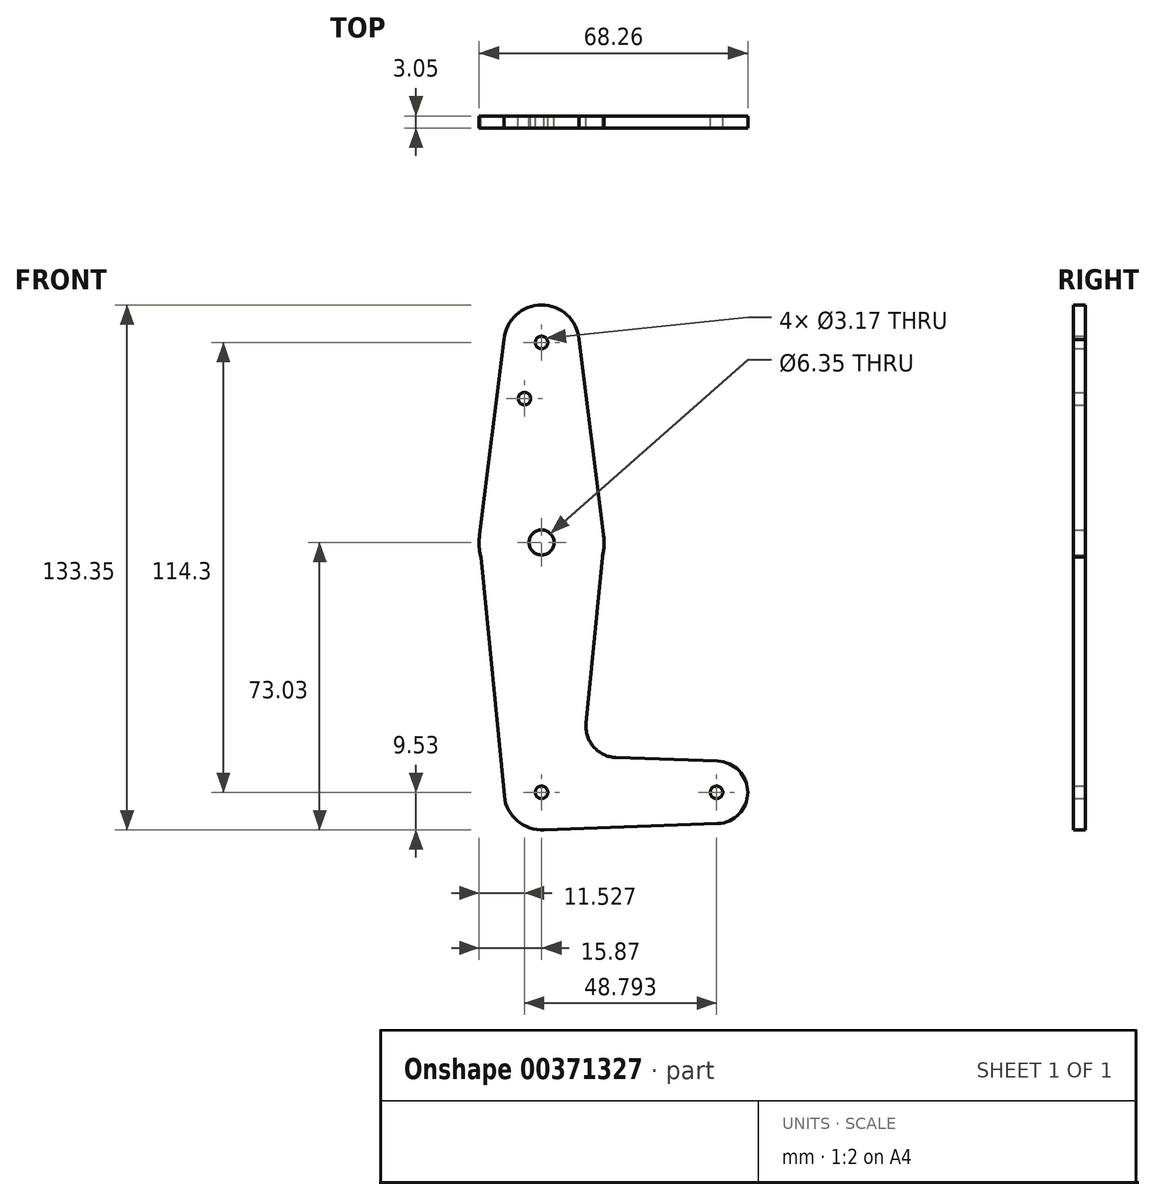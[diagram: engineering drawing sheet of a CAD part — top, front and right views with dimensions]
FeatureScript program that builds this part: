
annotation { "Feature Type Name" : "Feature", "Feature Type Description" : "" }
export const myFeature = defineFeature(function(context is Context, id is Id, definition is map)
    precondition{}
    {
        {
            var Q0;
            Q0=qCreatedBy(makeId("Front.planeOp"),FACE);
            var sketch = newSketch(context, id + "F0", { "sketchPlane" : qUnion([Q0])});
            skLineSegment(sketch, "E0", {"start": v(0, 50.8) * mm, "end": v(0, -63.5) * mm});
            skLineSegment(sketch, "E1", {"start": v(0, -63.5) * mm, "end": v(44.45, -63.5) * mm});
            skCircle(sketch, "E2", {"center": v(0, 0) * mm, "radius": 15.88 * mm});
            skCircle(sketch, "E3", {"center": v(0, 50.8) * mm, "radius": 9.53 * mm});
            skCircle(sketch, "E4", {"center": v(0, -63.5) * mm, "radius": 9.53 * mm});
            skCircle(sketch, "E5", {"center": v(44.45, -63.5) * mm, "radius": 7.94 * mm});
            skLineSegment(sketch, "E6", {"start": v(-9.4, 52.39) * mm, "end": v(-16, 0) * mm});
            skLineSegment(sketch, "E7", {"start": v(9.4, 52.39) * mm, "end": v(16, 0) * mm});
            skLineSegment(sketch, "E8", {"start": v(-15.44, -3.7) * mm, "end": v(-9.48, -64.43) * mm});
            skLineSegment(sketch, "E9", {"start": v(18.92, -54.65) * mm, "end": v(44.73, -55.57) * mm});
            skLineSegment(sketch, "E10", {"start": v(0, -73.02) * mm, "end": v(44.73, -71.43) * mm});
            skPoint(sketch, "E11.orphan", {"position": v(16, -3.7) * mm});
            skLineSegment(sketch, "E12.MirrorCS", {"start": v(15.44, -3.7) * mm, "end": v(11.3, -45.93) * mm});
            skCircle(sketch, "E13", {"center": v(-4.34, 36.53) * mm, "radius": 1.59 * mm});
            skCircle(sketch, "E14", {"center": v(0, 0) * mm, "radius": 3.18 * mm});
            skCircle(sketch, "E15", {"center": v(0, -63.5) * mm, "radius": 1.59 * mm});
            skCircle(sketch, "E16", {"center": v(44.45, -63.5) * mm, "radius": 1.59 * mm});
            skPoint(sketch, "E17.newPointB", {"position": v(9.48, -64.43) * mm});
            skArc(sketch, "E17.filletArc", {"start": v(11.3, -45.93) * mm, "mid": v(13.22, -51.94) * mm, "end": v(18.92, -54.65) * mm});
            skCircle(sketch, "E18", {"center": v(0, 50.8) * mm, "radius": 1.59 * mm});
            skSolve(sketch);
        }
        {
            var Q0;
            Q0 = qSketchRegion(id + "F0", true);
            var Q1;
            {var subQ0=sQuery(id+"F0.wireOp",EDGE,"E4");var subQ1=sQuery(id+"F0.wireOp",EDGE,"E0");var subQ2=makeQuery(id+"F0.imprint","INTERSECT",VERTEX,{"derivedFrom":[subQ1,subQ0]});Q1=makeQuery(id+"F0.imprint","IMPRINT",FACE,{"disambiguationData":[TD([[makeQuery(id+"F0.imprint","IMPRINT",EDGE,{"disambiguationData":[TD([[subQ2,-1.0]])],"derivedFrom":subQ1}),1.0]])]});}
            var Q2;
            {var subQ0=sQuery(id+"F0.wireOp",EDGE,"E4");var subQ1=sQuery(id+"F0.wireOp",EDGE,"E0");var subQ2=makeQuery(id+"F0.imprint","INTERSECT",VERTEX,{"derivedFrom":[subQ1,subQ0]});Q2=makeQuery(id+"F0.imprint","IMPRINT",FACE,{"disambiguationData":[TD([[makeQuery(id+"F0.imprint","IMPRINT",EDGE,{"disambiguationData":[TD([[subQ2,-1.0]])],"derivedFrom":subQ1}),1.0]])]});}
            extrude(context, id + "F1", {"entities" : qUnion([Q0, Q1, Q2]), "depth" : 3.05 * mm});
        }
    });
